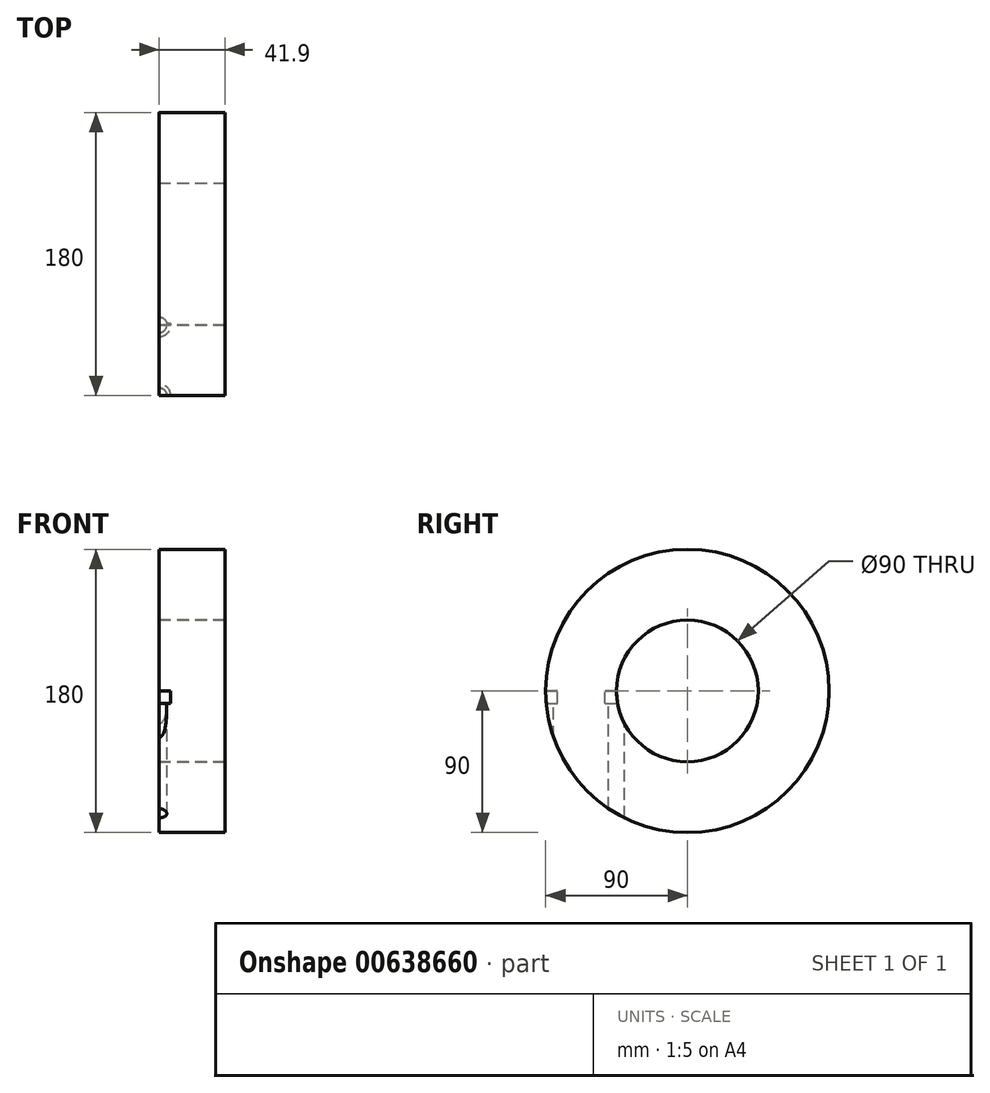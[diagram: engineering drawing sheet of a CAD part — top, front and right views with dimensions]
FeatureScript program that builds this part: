
annotation { "Feature Type Name" : "Feature", "Feature Type Description" : "" }
export const myFeature = defineFeature(function(context is Context, id is Id, definition is map)
    precondition{}
    {
        {
            var Q0;
            Q0=qCreatedBy(makeId("Top.planeOp"),FACE);
            var sketch = newSketch(context, id + "F0", { "sketchPlane" : qUnion([Q0])});
            skLineSegment(sketch, "E0.bottom", {"start": v(20.95, 22.5) * mm, "end": v(-20.95, 22.5) * mm});
            skLineSegment(sketch, "E0.top", {"start": v(20.95, -22.5) * mm, "end": v(-20.95, -22.5) * mm});
            skLineSegment(sketch, "E0.left", {"start": v(20.95, 22.5) * mm, "end": v(20.95, -22.5) * mm});
            skLineSegment(sketch, "E0.right", {"start": v(-20.95, 22.5) * mm, "end": v(-20.95, -22.5) * mm});
            skPoint(sketch, "E0.middle", {"position": v(0, 0) * mm});
            skArc(sketch, "E1.0.startCap", {"start": v(20.95, 67.5) * mm, "mid": v(65.95, 22.5) * mm, "end": v(20.95, -22.5) * mm});
            skArc(sketch, "E1.0.endCap", {"start": v(-20.95, -22.5) * mm, "mid": v(-65.95, 22.5) * mm, "end": v(-20.95, 67.5) * mm});
            skLineSegment(sketch, "E1.0.right", {"start": v(20.95, 67.5) * mm, "end": v(-20.95, 67.5) * mm});
            skSolve(sketch);
        }
        {
            var Q0;
            Q0=makeQuery(id+"F0.imprint","IMPRINT",FACE,{"disambiguationData":[TD([[makeQuery(id+"F0.imprint","IMPRINT",EDGE,{"derivedFrom":sQuery(id+"F0.wireOp",EDGE,"E0.bottom")}),1.0]])]});
            var Q1;
            Q1=sQuery(id+"F0.wireOp",EDGE,"E1.0.right");
            revolve(context, id + "F1", {"surfaceOperationType" : NewSurfaceOperationType.NEW, "entities" : qUnion([Q0]), "axis" : qUnion([Q1]), "revolveType" : RevolveType.ONE_DIRECTION, "oppositeDirection" : true, "angle" : 360 * degree});
        }
        {
            var Q0;
            Q0=makeQuery(id+"F0.imprint","IMPRINT",FACE,{"disambiguationData":[TD([[makeQuery(id+"F0.imprint","IMPRINT",EDGE,{"derivedFrom":sQuery(id+"F0.wireOp",EDGE,"E0.bottom")}),-1.0]])]});
            var Q1;
            Q1=sQuery(id+"F0.wireOp",EDGE,"E1.0.right");
            revolve(context, id + "F2", {"surfaceOperationType" : NewSurfaceOperationType.NEW, "entities" : qUnion([Q0]), "axis" : qUnion([Q1]), "revolveType" : RevolveType.FULL});
        }
        {
            var Q0;
            Q0=sQuery(id+"F0.wireOp",VERTEX,"E0.bottom.end");
            var Q1;
            Q1=sQuery(id+"F0.wireOp",VERTEX,"E0.top.end");
            var Q2;
            Q2=makeQuery(id+"F1.opRevolve","SWEPT_BODY",BODY,{"disambiguationData":[OSD([sQuery(id+"F0.wireOp",EDGE,"E0.bottom"),sQuery(id+"F0.wireOp",EDGE,"E0.left"),sQuery(id+"F0.wireOp",EDGE,"E0.right"),sQuery(id+"F0.wireOp",EDGE,"E0.top")])]});
            hole(context, id + "F3", {"style" : HoleStyle.C_BORE, "endStyle" : HoleEndStyle.THROUGH, "holeDiameter" : 10 * mm, "cBoreDiameter" : 15 * mm, "cBoreDepth" : 8 * mm, "majorDiameter" : 5 * mm, "isTappedThrough" : true, "tappedDepth" : 12 * mm, "tapClearance" : 3, "locations" : qUnion([Q0, Q1]), "scope" : qUnion([Q2])});
        }
    });
